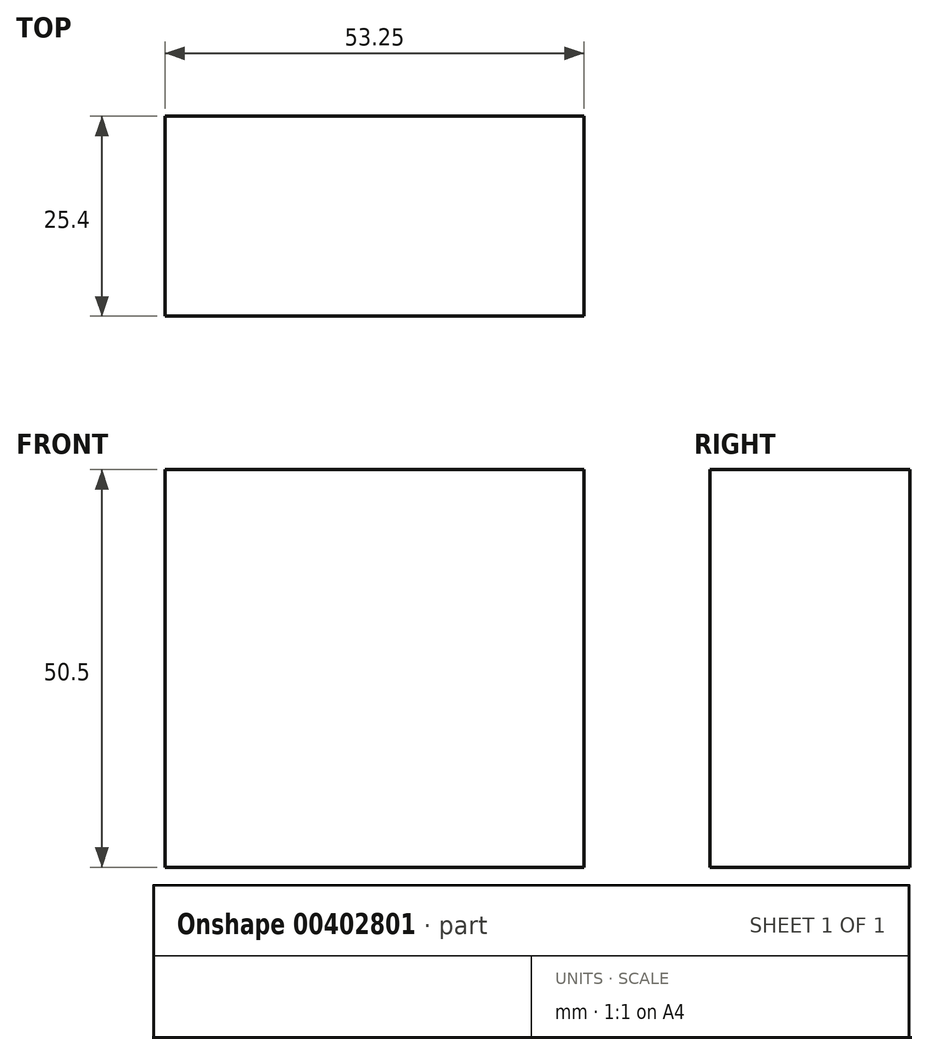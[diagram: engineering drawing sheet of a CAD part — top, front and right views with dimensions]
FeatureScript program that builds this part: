
annotation { "Feature Type Name" : "Feature", "Feature Type Description" : "" }
export const myFeature = defineFeature(function(context is Context, id is Id, definition is map)
    precondition{}
    {
        {
            var Q0;
            Q0=qCreatedBy(makeId("Front.planeOp"),FACE);
            var sketch = newSketch(context, id + "F0", { "sketchPlane" : qUnion([Q0])});
            skLineSegment(sketch, "E0.bottom", {"start": v(1.92, -2.88) * mm, "end": v(-51.33, -2.88) * mm});
            skLineSegment(sketch, "E0.top", {"start": v(1.92, 47.62) * mm, "end": v(-51.33, 47.62) * mm});
            skLineSegment(sketch, "E0.left", {"start": v(1.92, -2.88) * mm, "end": v(1.92, 47.62) * mm});
            skLineSegment(sketch, "E0.right", {"start": v(-51.33, -2.88) * mm, "end": v(-51.33, 47.62) * mm});
            skSolve(sketch);
        }
        {
            var Q0;
            Q0 = qSketchRegion(id + "F0", true);
            extrude(context, id + "F1", {"entities" : qUnion([Q0]), "depth" : 25.4 * mm});
        }
    });
